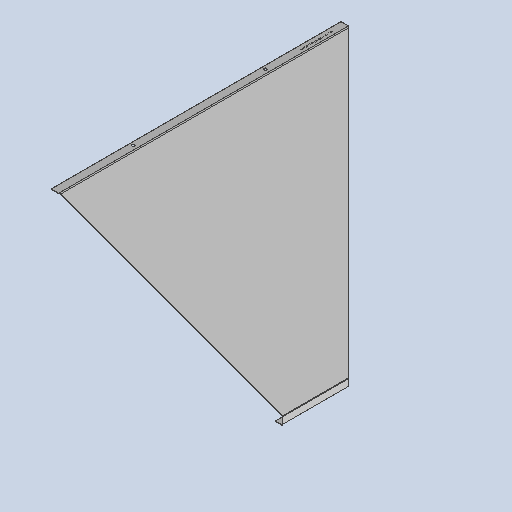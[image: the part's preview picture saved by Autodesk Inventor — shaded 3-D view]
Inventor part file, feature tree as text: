
AUTODESK INVENTOR PART (.ipt)
format: ipt  version: 2025 (Build 290162010, 162A)  size: 421,376 bytes
history: native  units: mm
features: sheet_metal_op x9, other x8, sketch x8, extrude x2, mirror x1, pattern_linear x1, projected_geometry x1
ambient origin geometry x8: Origin, YZ Plane, XZ Plane, XY Plane, X Axis, Y Axis, Z Axis, Center Point
bodies: Solid1 (feature_tree)
feature tree (30):
  sheet_metal_op  "Contour Flange1"
  extrude  "Extrusion6"  Depth=3.0mm
  other  "Mark2"
  other  "A-Side Definition"
  extrude  "Extrusion12"  Depth=6.0mm
  mirror  "Mirror1"
  sheet_metal_op  "Flange3"
  sheet_metal_op  "Flange4"
  pattern_linear  "Rectangular Pattern1"  Count1=174  [1 undecoded]
  sketch  "Sketch1"  dims[d6=3.0mm d7=3.0mm]
  other  "Plate1"
  sheet_metal_op  "Bend1"
  sheet_metal_op  "Corner1"
  sketch  "Sketch9"  dims[d8=1.5mm d9=6.0mm]
  sketch  "Sketch16"  dims[d10=5.0mm d11=1740.0mm]
  sketch  "Sketch17"  dims[d12=5.0mm]
  projected_geometry  "Projected Loop8"
  sketch  "Sketch18"  dims[d13=4.0mm]
  other  "Plate4"
  sheet_metal_op  "Bend4"
  sheet_metal_op  "Corner4"
  sketch  "Sketch19"  dims[d14=12.0mm]
  other  "Plate5"
  sheet_metal_op  "Bend5"
  sheet_metal_op  "Corner5"
  sketch  "Sketch20"  dims[d15=3.0mm]
  sketch  "Sketch21"  dims[d16=5.0mm d62=0.0mm d63=1170.0mm d64=8.0mm d68=10.0mm d69=0.0mm d93=400.0mm d97=3.0mm d98=120.0deg d99=8.0mm d100=0.0mm d101=175.0mm d103=850.499815mm d104=50.0mm d105=3.0mm d106=1.5mm d107=6.0mm d108=5.0mm d109=50.0mm d110=30.0deg d111=5.0mm d112=12.0mm d113=3.0mm d114=5.0mm d115=3.0mm d116=1.5mm d117=6.0mm d118=5.0mm d119=45.0mm d120=90.0deg d121=5.0mm d122=12.0mm d123=3.0mm d124=5.0mm d125=20.0mm d126=16.0mm d127=3.0mm d128=0.0mm d129=30.0mm d131=160.0mm d132=16.0mm d133=20.0mm d134=800.0mm d135=3.0mm d136=0.0mm]
  other  "Cut1"
  other  "Cut2"
  other  "Definition1"
note: 1 required parameter value undecoded (feature->parameter linkage not recoverable at this tier; creation-order binding heuristic only, values carry confidence <= 0.55)
